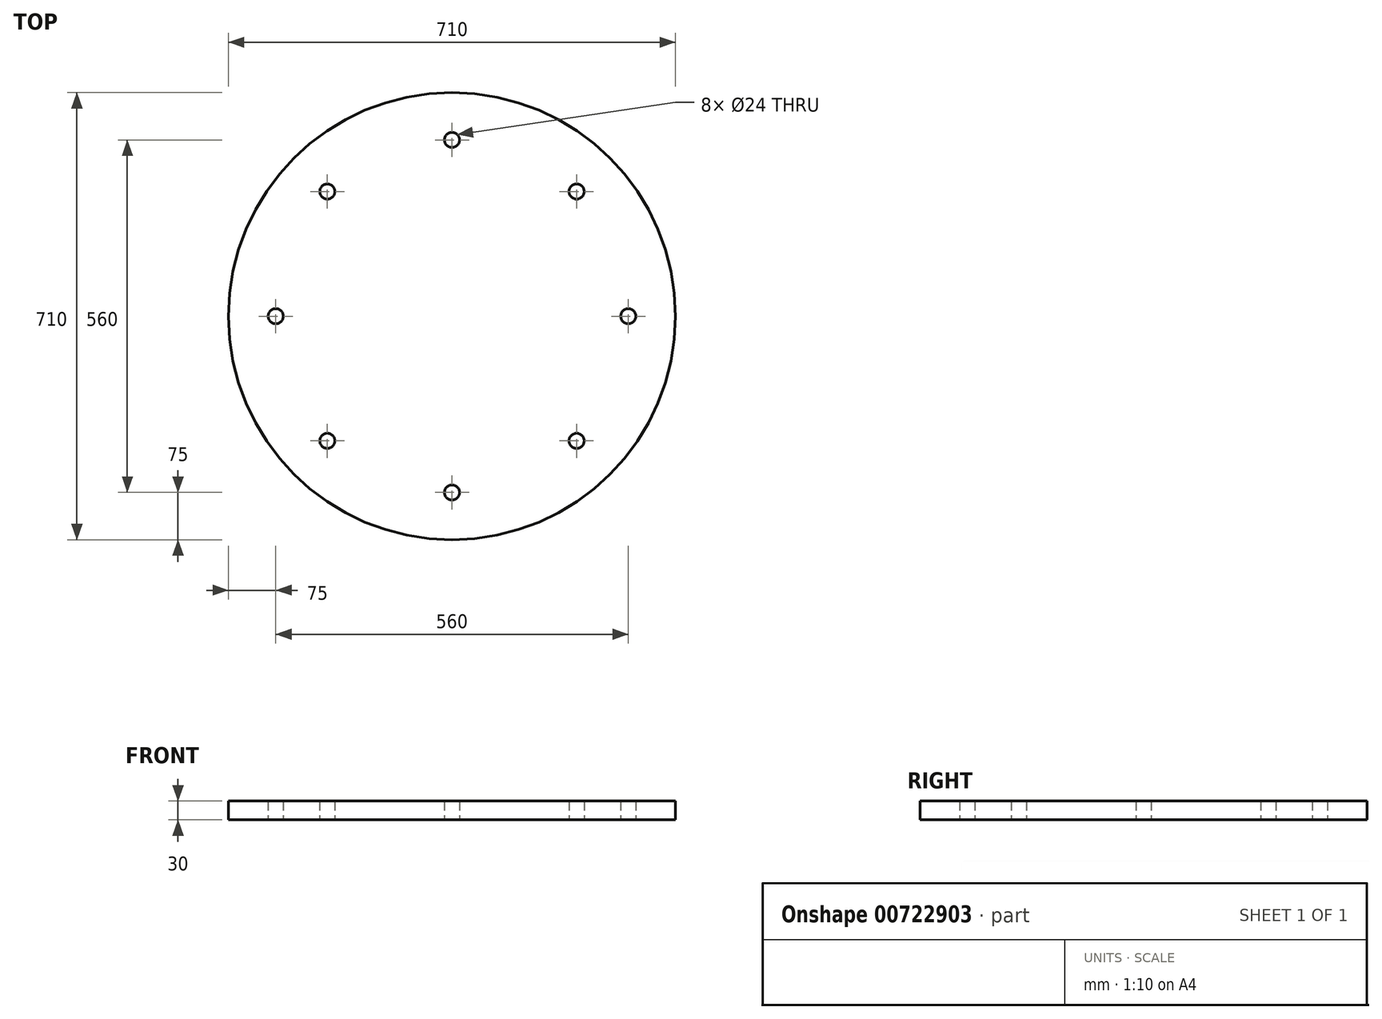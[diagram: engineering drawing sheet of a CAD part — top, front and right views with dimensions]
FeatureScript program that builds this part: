
annotation { "Feature Type Name" : "Feature", "Feature Type Description" : "" }
export const myFeature = defineFeature(function(context is Context, id is Id, definition is map)
    precondition{}
    {
        {
            var Q0;
            Q0=qCreatedBy(makeId("Top.planeOp"),FACE);
            var sketch = newSketch(context, id + "F0", { "sketchPlane" : qUnion([Q0])});
            skCircle(sketch, "E0", {"center": v(0, 0) * mm, "radius": 355 * mm});
            skLineSegment(sketch, "E1", {"start": v(0, 0) * mm, "end": v(280, 0) * mm});
            skLineSegment(sketch, "E2", {"start": v(0, 0) * mm, "end": v(-280, 0) * mm});
            skCircle(sketch, "E3", {"center": v(280, 0) * mm, "radius": 12 * mm});
            skCircle(sketch, "E4", {"center": v(-280, 0) * mm, "radius": 12 * mm});
            skCircle(sketch, "E5.1.0", {"center": v(197.99, 197.99) * mm, "radius": 12 * mm});
            skCircle(sketch, "E5.2.0", {"center": v(0, 280) * mm, "radius": 12 * mm});
            skCircle(sketch, "E5.3.0", {"center": v(-197.99, 197.99) * mm, "radius": 12 * mm});
            skCircle(sketch, "E5.5.0", {"center": v(-197.99, -197.99) * mm, "radius": 12 * mm});
            skCircle(sketch, "E5.6.0", {"center": v(0, -280) * mm, "radius": 12 * mm});
            skCircle(sketch, "E5.7.0", {"center": v(197.99, -197.99) * mm, "radius": 12 * mm});
            skSolve(sketch);
        }
        {
            var Q0;
            Q0=makeQuery(id+"F0.imprint","IMPRINT",FACE,{"disambiguationData":[TD([[makeQuery(id+"F0.imprint","IMPRINT",EDGE,{"derivedFrom":sQuery(id+"F0.wireOp",EDGE,"E0")}),1.0]])]});
            extrude(context, id + "F1", {"entities" : qUnion([Q0]), "depth" : 30 * mm, "offsetDistance" : 25 * mm});
        }
    });
